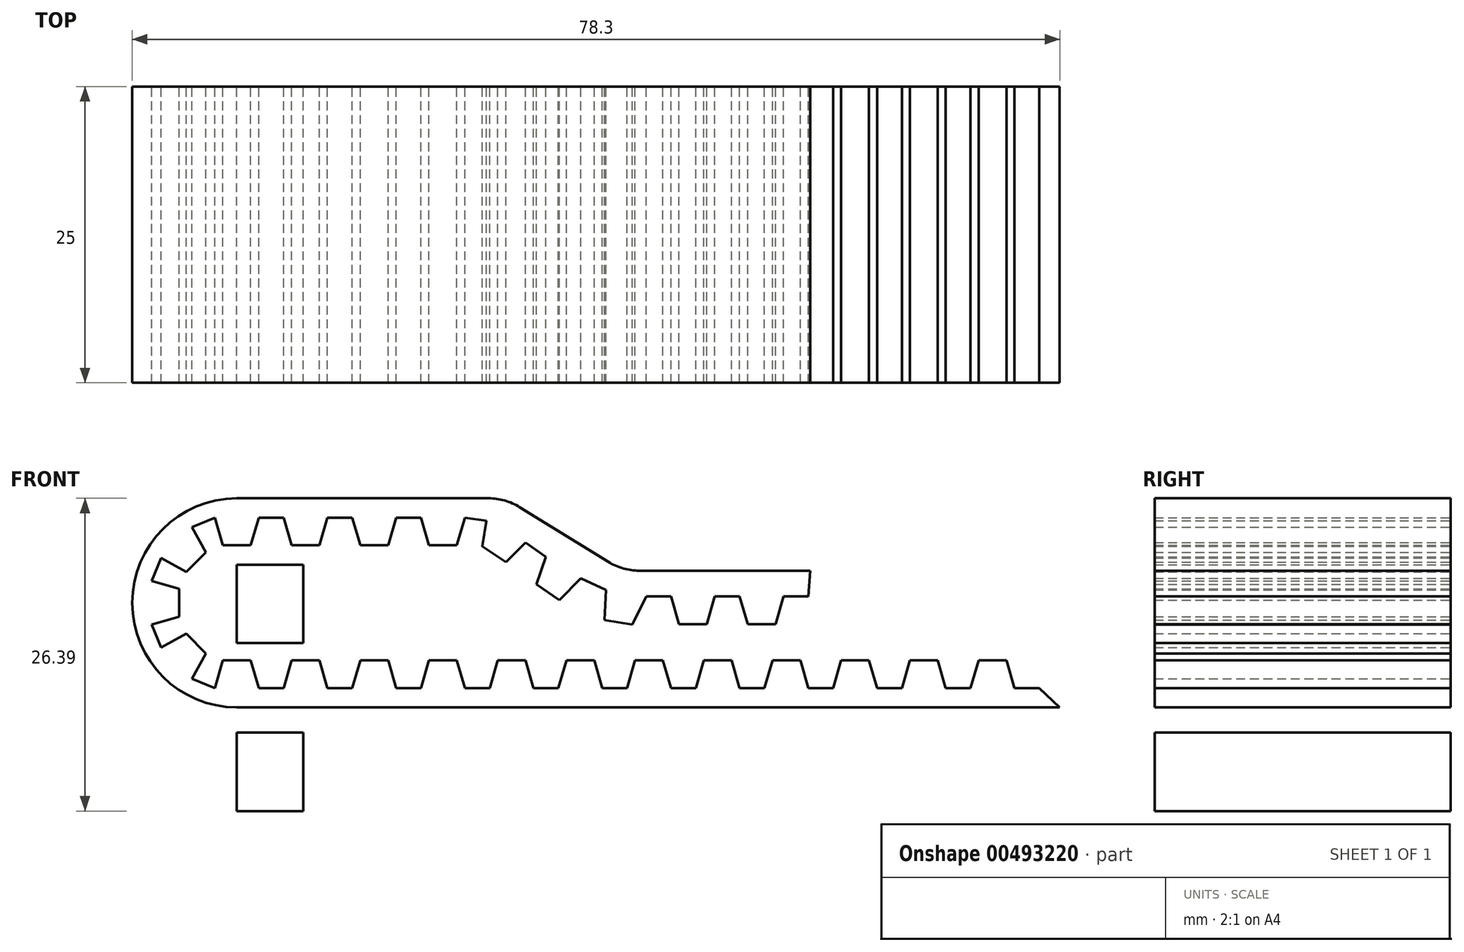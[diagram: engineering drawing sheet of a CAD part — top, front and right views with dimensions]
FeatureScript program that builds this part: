
annotation { "Feature Type Name" : "Feature", "Feature Type Description" : "" }
export const myFeature = defineFeature(function(context is Context, id is Id, definition is map)
    precondition{}
    {
        {
            var Q0;
            Q0=qCreatedBy(makeId("Front.planeOp"),FACE);
            var sketch = newSketch(context, id + "F0", { "sketchPlane" : qUnion([Q0])});
            skLineSegment(sketch, "E0.bottom", {"start": v(-2.81, 12.05) * mm, "end": v(2.81, 12.05) * mm});
            skLineSegment(sketch, "E0.top", {"start": v(-2.81, 5.44) * mm, "end": v(2.81, 5.44) * mm});
            skLineSegment(sketch, "E0.left", {"start": v(-2.81, 12.05) * mm, "end": v(-2.81, 5.44) * mm});
            skLineSegment(sketch, "E0.right", {"start": v(2.81, 12.05) * mm, "end": v(2.81, 5.44) * mm});
            skPoint(sketch, "E0.middle", {"position": v(0, 8.74) * mm});
            skLineSegment(sketch, "E1.MirrorCS", {"start": v(2.81, -8.75) * mm, "end": v(2.81, -2.14) * mm});
            skLineSegment(sketch, "E2.MirrorCS", {"start": v(-2.81, -8.75) * mm, "end": v(-2.81, -2.14) * mm});
            skLineSegment(sketch, "E3.MirrorCS", {"start": v(-2.81, -2.14) * mm, "end": v(2.81, -2.14) * mm});
            skLineSegment(sketch, "E4.MirrorCS", {"start": v(-2.81, -8.75) * mm, "end": v(2.81, -8.75) * mm});
            skLineSegment(sketch, "E5", {"start": v(-2.81, 17.64) * mm, "end": v(18.44, 17.64) * mm});
            skArc(sketch, "E6", {"start": v(-2.81, 17.64) * mm, "mid": v(-11.63, 8.82) * mm, "end": v(-2.81, 0) * mm});
            skLineSegment(sketch, "E7", {"start": v(-1.63, 13.68) * mm, "end": v(-3.99, 13.68) * mm});
            skPoint(sketch, "E8", {"position": v(-2.81, 13.68) * mm});
            skLineSegment(sketch, "E9", {"start": v(-1.63, 13.68) * mm, "end": v(-0.96, 16.02) * mm});
            skLineSegment(sketch, "E10", {"start": v(-3.99, 13.68) * mm, "end": v(-4.66, 16.02) * mm});
            skLineSegment(sketch, "E11.1.0", {"start": v(-5.41, 13.1) * mm, "end": v(-7.08, 11.43) * mm});
            skLineSegment(sketch, "E11.1.1", {"start": v(-7.08, 11.43) * mm, "end": v(-9.2, 12.6) * mm});
            skPoint(sketch, "E11.1.2", {"position": v(-6.25, 12.26) * mm});
            skLineSegment(sketch, "E11.1.3", {"start": v(-5.41, 13.1) * mm, "end": v(-6.6, 15.22) * mm});
            skLineSegment(sketch, "E11.2.0", {"start": v(-7.67, 10) * mm, "end": v(-7.67, 7.65) * mm});
            skLineSegment(sketch, "E11.2.1", {"start": v(-7.67, 7.65) * mm, "end": v(-10, 6.97) * mm});
            skPoint(sketch, "E11.2.2", {"position": v(-7.67, 8.82) * mm});
            skLineSegment(sketch, "E11.2.3", {"start": v(-7.67, 10) * mm, "end": v(-10, 10.67) * mm});
            skLineSegment(sketch, "E11.3.0", {"start": v(-7.08, 6.22) * mm, "end": v(-5.41, 4.55) * mm});
            skLineSegment(sketch, "E11.3.1", {"start": v(-5.41, 4.55) * mm, "end": v(-6.6, 2.42) * mm});
            skPoint(sketch, "E11.3.2", {"position": v(-6.25, 5.39) * mm});
            skLineSegment(sketch, "E11.3.3", {"start": v(-7.08, 6.22) * mm, "end": v(-9.2, 5.04) * mm});
            skLineSegment(sketch, "E11.4.0", {"start": v(-3.99, 3.96) * mm, "end": v(-1.63, 3.96) * mm});
            skLineSegment(sketch, "E11.4.1", {"start": v(-1.63, 3.96) * mm, "end": v(-0.96, 1.63) * mm});
            skPoint(sketch, "E11.4.2", {"position": v(-2.81, 3.96) * mm});
            skLineSegment(sketch, "E11.4.3", {"start": v(-3.99, 3.96) * mm, "end": v(-4.66, 1.63) * mm});
            skLineSegment(sketch, "E12", {"start": v(-4.66, 16.02) * mm, "end": v(-6.6, 15.22) * mm});
            skLineSegment(sketch, "E13", {"start": v(-9.2, 12.6) * mm, "end": v(-10, 10.67) * mm});
            skLineSegment(sketch, "E14", {"start": v(-10, 6.97) * mm, "end": v(-9.2, 5.04) * mm});
            skLineSegment(sketch, "E15", {"start": v(-6.6, 2.42) * mm, "end": v(-4.66, 1.63) * mm});
            skLineSegment(sketch, "E16", {"start": v(-0.96, 16.02) * mm, "end": v(1.14, 16.02) * mm});
            skLineSegment(sketch, "E17", {"start": v(-0.96, 1.63) * mm, "end": v(1.14, 1.63) * mm});
            skPoint(sketch, "E18.1.0.0", {"position": v(2.99, 3.96) * mm});
            skLineSegment(sketch, "E18.1.0.1", {"start": v(4.17, 3.96) * mm, "end": v(4.84, 1.63) * mm});
            skLineSegment(sketch, "E18.1.0.2", {"start": v(4.84, 1.63) * mm, "end": v(6.94, 1.63) * mm});
            skLineSegment(sketch, "E18.1.0.3", {"start": v(1.81, 3.96) * mm, "end": v(1.14, 1.63) * mm});
            skLineSegment(sketch, "E18.1.0.4", {"start": v(1.81, 13.68) * mm, "end": v(1.14, 16.02) * mm});
            skLineSegment(sketch, "E18.1.0.5", {"start": v(4.17, 13.68) * mm, "end": v(1.81, 13.68) * mm});
            skLineSegment(sketch, "E18.1.0.6", {"start": v(4.17, 13.68) * mm, "end": v(4.84, 16.02) * mm});
            skLineSegment(sketch, "E18.1.0.7", {"start": v(1.81, 3.96) * mm, "end": v(4.17, 3.96) * mm});
            skPoint(sketch, "E18.1.0.8", {"position": v(2.99, 13.68) * mm});
            skLineSegment(sketch, "E18.1.0.9", {"start": v(4.84, 16.02) * mm, "end": v(6.94, 16.02) * mm});
            skPoint(sketch, "E18.2.0.0", {"position": v(8.79, 3.96) * mm});
            skLineSegment(sketch, "E18.2.0.1", {"start": v(9.97, 3.96) * mm, "end": v(10.64, 1.63) * mm});
            skLineSegment(sketch, "E18.2.0.2", {"start": v(10.64, 1.63) * mm, "end": v(12.74, 1.63) * mm});
            skLineSegment(sketch, "E18.2.0.3", {"start": v(7.61, 3.96) * mm, "end": v(6.94, 1.63) * mm});
            skLineSegment(sketch, "E18.2.0.4", {"start": v(7.61, 13.68) * mm, "end": v(6.94, 16.02) * mm});
            skLineSegment(sketch, "E18.2.0.5", {"start": v(9.97, 13.68) * mm, "end": v(7.61, 13.68) * mm});
            skLineSegment(sketch, "E18.2.0.6", {"start": v(9.97, 13.68) * mm, "end": v(10.64, 16.02) * mm});
            skLineSegment(sketch, "E18.2.0.7", {"start": v(7.61, 3.96) * mm, "end": v(9.97, 3.96) * mm});
            skPoint(sketch, "E18.2.0.8", {"position": v(8.79, 13.68) * mm});
            skLineSegment(sketch, "E18.2.0.9", {"start": v(10.64, 16.02) * mm, "end": v(12.74, 16.02) * mm});
            skPoint(sketch, "E18.3.0.0", {"position": v(14.59, 3.96) * mm});
            skLineSegment(sketch, "E18.3.0.1", {"start": v(15.77, 3.96) * mm, "end": v(16.44, 1.63) * mm});
            skLineSegment(sketch, "E18.3.0.2", {"start": v(16.44, 1.63) * mm, "end": v(18.54, 1.63) * mm});
            skLineSegment(sketch, "E18.3.0.3", {"start": v(13.41, 3.96) * mm, "end": v(12.74, 1.63) * mm});
            skLineSegment(sketch, "E18.3.0.4", {"start": v(13.41, 13.68) * mm, "end": v(12.74, 16.02) * mm});
            skLineSegment(sketch, "E18.3.0.5", {"start": v(15.77, 13.68) * mm, "end": v(13.41, 13.68) * mm});
            skLineSegment(sketch, "E18.3.0.6", {"start": v(15.77, 13.68) * mm, "end": v(16.44, 16.02) * mm});
            skLineSegment(sketch, "E18.3.0.7", {"start": v(13.41, 3.96) * mm, "end": v(15.77, 3.96) * mm});
            skPoint(sketch, "E18.3.0.8", {"position": v(14.59, 13.68) * mm});
            skLineSegment(sketch, "E18.3.0.9", {"start": v(16.44, 16.02) * mm, "end": v(18.25, 15.76) * mm});
            skPoint(sketch, "E18.4.0.0", {"position": v(20.39, 3.96) * mm});
            skLineSegment(sketch, "E18.4.0.1", {"start": v(21.57, 3.96) * mm, "end": v(22.24, 1.63) * mm});
            skLineSegment(sketch, "E18.4.0.2", {"start": v(22.24, 1.63) * mm, "end": v(24.34, 1.63) * mm});
            skLineSegment(sketch, "E18.4.0.3", {"start": v(19.21, 3.96) * mm, "end": v(18.54, 1.63) * mm});
            skLineSegment(sketch, "E18.4.0.4", {"start": v(17.9, 13.58) * mm, "end": v(18.25, 15.76) * mm});
            skLineSegment(sketch, "E18.4.0.5", {"start": v(19.92, 12.26) * mm, "end": v(17.9, 13.58) * mm});
            skLineSegment(sketch, "E18.4.0.6", {"start": v(19.92, 12.26) * mm, "end": v(21.57, 13.9) * mm});
            skLineSegment(sketch, "E18.4.0.7", {"start": v(19.21, 3.96) * mm, "end": v(21.57, 3.96) * mm});
            skLineSegment(sketch, "E18.4.0.9", {"start": v(21.57, 13.9) * mm, "end": v(23.29, 12.7) * mm});
            skPoint(sketch, "E18.5.0.0", {"position": v(26.19, 3.96) * mm});
            skLineSegment(sketch, "E18.5.0.1", {"start": v(27.37, 3.96) * mm, "end": v(28.04, 1.63) * mm});
            skLineSegment(sketch, "E18.5.0.2", {"start": v(28.04, 1.63) * mm, "end": v(30.14, 1.63) * mm});
            skLineSegment(sketch, "E18.5.0.3", {"start": v(25.01, 3.96) * mm, "end": v(24.34, 1.63) * mm});
            skLineSegment(sketch, "E18.5.0.4", {"start": v(22.5, 10.4) * mm, "end": v(23.29, 12.7) * mm});
            skLineSegment(sketch, "E18.5.0.5", {"start": v(24.43, 9.04) * mm, "end": v(22.5, 10.4) * mm});
            skLineSegment(sketch, "E18.5.0.6", {"start": v(24.43, 9.04) * mm, "end": v(26.23, 10.88) * mm});
            skLineSegment(sketch, "E18.5.0.7", {"start": v(25.01, 3.96) * mm, "end": v(27.37, 3.96) * mm});
            skLineSegment(sketch, "E18.5.0.9", {"start": v(26.23, 10.88) * mm, "end": v(28.36, 9.9) * mm});
            skPoint(sketch, "E18.6.0.0", {"position": v(31.99, 3.96) * mm});
            skLineSegment(sketch, "E18.6.0.1", {"start": v(33.17, 3.96) * mm, "end": v(33.84, 1.63) * mm});
            skLineSegment(sketch, "E18.6.0.2", {"start": v(33.84, 1.63) * mm, "end": v(35.94, 1.63) * mm});
            skLineSegment(sketch, "E18.6.0.3", {"start": v(30.81, 3.96) * mm, "end": v(30.14, 1.63) * mm});
            skLineSegment(sketch, "E18.6.0.4", {"start": v(28.24, 7.38) * mm, "end": v(28.36, 9.9) * mm});
            skLineSegment(sketch, "E18.6.0.5", {"start": v(30.6, 6.98) * mm, "end": v(28.24, 7.38) * mm});
            skLineSegment(sketch, "E18.6.0.6", {"start": v(30.6, 6.98) * mm, "end": v(31.74, 9.36) * mm});
            skLineSegment(sketch, "E18.6.0.7", {"start": v(30.81, 3.96) * mm, "end": v(33.17, 3.96) * mm});
            skLineSegment(sketch, "E18.6.0.9", {"start": v(31.74, 9.36) * mm, "end": v(33.84, 9.36) * mm});
            skPoint(sketch, "E18.7.0.0", {"position": v(37.79, 3.96) * mm});
            skLineSegment(sketch, "E18.7.0.1", {"start": v(38.97, 3.96) * mm, "end": v(39.64, 1.63) * mm});
            skLineSegment(sketch, "E18.7.0.2", {"start": v(39.64, 1.63) * mm, "end": v(41.74, 1.63) * mm});
            skLineSegment(sketch, "E18.7.0.3", {"start": v(36.61, 3.96) * mm, "end": v(35.94, 1.63) * mm});
            skLineSegment(sketch, "E18.7.0.4", {"start": v(34.52, 7.03) * mm, "end": v(33.84, 9.36) * mm});
            skLineSegment(sketch, "E18.7.0.5", {"start": v(36.87, 7.03) * mm, "end": v(34.52, 7.03) * mm});
            skLineSegment(sketch, "E18.7.0.6", {"start": v(36.87, 7.03) * mm, "end": v(37.54, 9.36) * mm});
            skLineSegment(sketch, "E18.7.0.7", {"start": v(36.61, 3.96) * mm, "end": v(38.97, 3.96) * mm});
            skLineSegment(sketch, "E18.7.0.9", {"start": v(37.54, 9.36) * mm, "end": v(39.64, 9.36) * mm});
            skPoint(sketch, "E18.8.0.0", {"position": v(43.59, 3.96) * mm});
            skLineSegment(sketch, "E18.8.0.1", {"start": v(44.77, 3.96) * mm, "end": v(45.44, 1.63) * mm});
            skLineSegment(sketch, "E18.8.0.2", {"start": v(45.44, 1.63) * mm, "end": v(47.54, 1.63) * mm});
            skLineSegment(sketch, "E18.8.0.3", {"start": v(42.41, 3.96) * mm, "end": v(41.74, 1.63) * mm});
            skLineSegment(sketch, "E18.8.0.4", {"start": v(40.32, 7.03) * mm, "end": v(39.64, 9.36) * mm});
            skLineSegment(sketch, "E18.8.0.5", {"start": v(42.67, 7.03) * mm, "end": v(40.32, 7.03) * mm});
            skLineSegment(sketch, "E18.8.0.6", {"start": v(42.67, 7.03) * mm, "end": v(43.34, 9.36) * mm});
            skLineSegment(sketch, "E18.8.0.7", {"start": v(42.41, 3.96) * mm, "end": v(44.77, 3.96) * mm});
            skLineSegment(sketch, "E18.8.0.9", {"start": v(43.34, 9.36) * mm, "end": v(45.44, 9.36) * mm});
            skPoint(sketch, "E18.9.0.0", {"position": v(49.39, 3.96) * mm});
            skLineSegment(sketch, "E18.9.0.1", {"start": v(50.57, 3.96) * mm, "end": v(51.24, 1.63) * mm});
            skLineSegment(sketch, "E18.9.0.2", {"start": v(51.24, 1.63) * mm, "end": v(53.34, 1.63) * mm});
            skLineSegment(sketch, "E18.9.0.3", {"start": v(48.21, 3.96) * mm, "end": v(47.54, 1.63) * mm});
            skLineSegment(sketch, "E18.9.0.7", {"start": v(48.21, 3.96) * mm, "end": v(50.57, 3.96) * mm});
            skPoint(sketch, "E18.10.0.0", {"position": v(55.19, 3.96) * mm});
            skLineSegment(sketch, "E18.10.0.1", {"start": v(56.37, 3.96) * mm, "end": v(57.04, 1.63) * mm});
            skLineSegment(sketch, "E18.10.0.2", {"start": v(57.04, 1.63) * mm, "end": v(59.14, 1.63) * mm});
            skLineSegment(sketch, "E18.10.0.3", {"start": v(54.01, 3.96) * mm, "end": v(53.34, 1.63) * mm});
            skLineSegment(sketch, "E18.10.0.7", {"start": v(54.01, 3.96) * mm, "end": v(56.37, 3.96) * mm});
            skPoint(sketch, "E18.11.0.0", {"position": v(60.99, 3.96) * mm});
            skLineSegment(sketch, "E18.11.0.1", {"start": v(62.17, 3.96) * mm, "end": v(62.84, 1.63) * mm});
            skLineSegment(sketch, "E18.11.0.2", {"start": v(62.84, 1.63) * mm, "end": v(64.94, 1.63) * mm});
            skLineSegment(sketch, "E18.11.0.3", {"start": v(59.81, 3.96) * mm, "end": v(59.14, 1.63) * mm});
            skLineSegment(sketch, "E18.11.0.7", {"start": v(59.81, 3.96) * mm, "end": v(62.17, 3.96) * mm});
            skLineSegment(sketch, "E19", {"start": v(64.94, 1.63) * mm, "end": v(66.67, 0) * mm});
            skLineSegment(sketch, "E20", {"start": v(-2.81, 0) * mm, "end": v(66.67, 0) * mm});
            skLineSegment(sketch, "E21", {"start": v(21.07, 16.9) * mm, "end": v(28.55, 12.28) * mm});
            skLineSegment(sketch, "E22", {"start": v(31.18, 11.54) * mm, "end": v(45.6, 11.54) * mm});
            skLineSegment(sketch, "E23", {"start": v(45.6, 11.54) * mm, "end": v(45.44, 9.36) * mm});
            skPoint(sketch, "E24.visualSharp", {"position": v(19.86, 17.64) * mm});
            skArc(sketch, "E24.filletArc", {"start": v(21.07, 16.9) * mm, "mid": v(19.8, 17.45) * mm, "end": v(18.44, 17.64) * mm});
            skPoint(sketch, "E25.visualSharp", {"position": v(29.76, 11.54) * mm});
            skArc(sketch, "E25.filletArc", {"start": v(28.55, 12.28) * mm, "mid": v(29.81, 11.73) * mm, "end": v(31.18, 11.54) * mm});
            skSolve(sketch);
        }
        {
            var Q0;
            Q0 = qSketchRegion(id + "F0", true);
            extrude(context, id + "F1", {"entities" : qUnion([Q0]), "depth" : 25 * mm});
        }
    });
